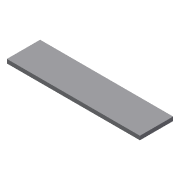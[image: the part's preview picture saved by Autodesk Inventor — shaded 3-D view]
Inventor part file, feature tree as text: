
AUTODESK INVENTOR PART (.ipt)
format: ipt  version: 2014 (Build 180170000, 170)  size: 66,048 bytes
history: native  units: mm
features: extrude x1, sketch x1
ambient origin geometry x8: Origin, YZ Plane, XZ Plane, XY Plane, X Axis, Y Axis, Z Axis, Center Point
bodies: Solid1 (feature_tree)
feature tree (2):
  extrude  "Extrusion1"  Depth=101.6mm
  sketch  "Sketch1"  dims[d0=25.4mm d1=101.6mm d2=3.0mm d3=0.0mm]
